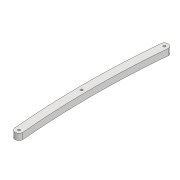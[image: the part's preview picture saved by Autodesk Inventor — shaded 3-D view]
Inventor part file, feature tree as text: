
AUTODESK INVENTOR PART (.ipt)
format: ipt  version: 2022 (Build 260153000, 153)  size: 98,304 bytes
history: native  units: mm
features: extrude x1, other x1
ambient origin geometry x8: Origin, YZ Plane, XZ Plane, XY Plane, X Axis, Y Axis, Z Axis, Center Point
bodies: Solid1 (feature_tree)
feature tree (2):
  extrude  "Extrusion1"  Depth=183.747mm
  other  "Work Axis1"
